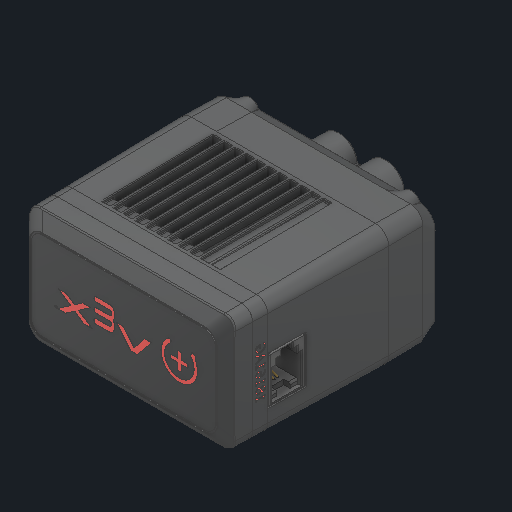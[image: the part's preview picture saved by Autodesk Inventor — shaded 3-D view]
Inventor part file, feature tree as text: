
AUTODESK INVENTOR PART (.ipt)
format: ipt  version: 2025 (Build 290162000, 162)  size: 13,122,560 bytes
history: native  units: in
note: dims shown in document units (in); Inventor stores cm internally (conversion verified against a paired STEP export)
features: other x19, sketch x2
ambient origin geometry x8: Origin, YZ Plane, XZ Plane, XY Plane, X Axis, Y Axis, Z Axis, Center Point
bodies: Solid1 (feature_tree), Solid2 (feature_tree), Solid7 (feature_tree), Solid8 (feature_tree), Solid9 (feature_tree), Solid20 (feature_tree), Solid21 (feature_tree), Solid22 (feature_tree)
feature tree (21):
  other  "V5 Motor.ipt"
  other  "Solid1::V5 Motor.ipt"
  other  "Solid2::V5 Motor.ipt"
  other  "Solid4::V5 Motor.ipt"
  other  "Solid6::V5 Motor.ipt"
  other  "Solid7::V5 Motor.ipt"
  other  "Solid8::V5 Motor.ipt"
  other  "Solid9::V5 Motor.ipt"
  other  "Solid14::V5 Motor.ipt"
  other  "Solid16::V5 Motor.ipt"
  other  "Solid17::V5 Motor.ipt"
  other  "Solid18::V5 Motor.ipt"
  other  "Solid19::V5 Motor.ipt"
  other  "Solid20::V5 Motor.ipt"
  other  "Solid21::V5 Motor.ipt"
  other  "Solid22::V5 Motor.ipt"
  other  "TaggingFeature1"
  sketch  "Sketch1"  dims[d0=0.3937in]
  sketch  "Sketch2"  dims[d4=0.0in d5=0.0in]
  other  "iInsert:1"
  other  "iInsert:2"
